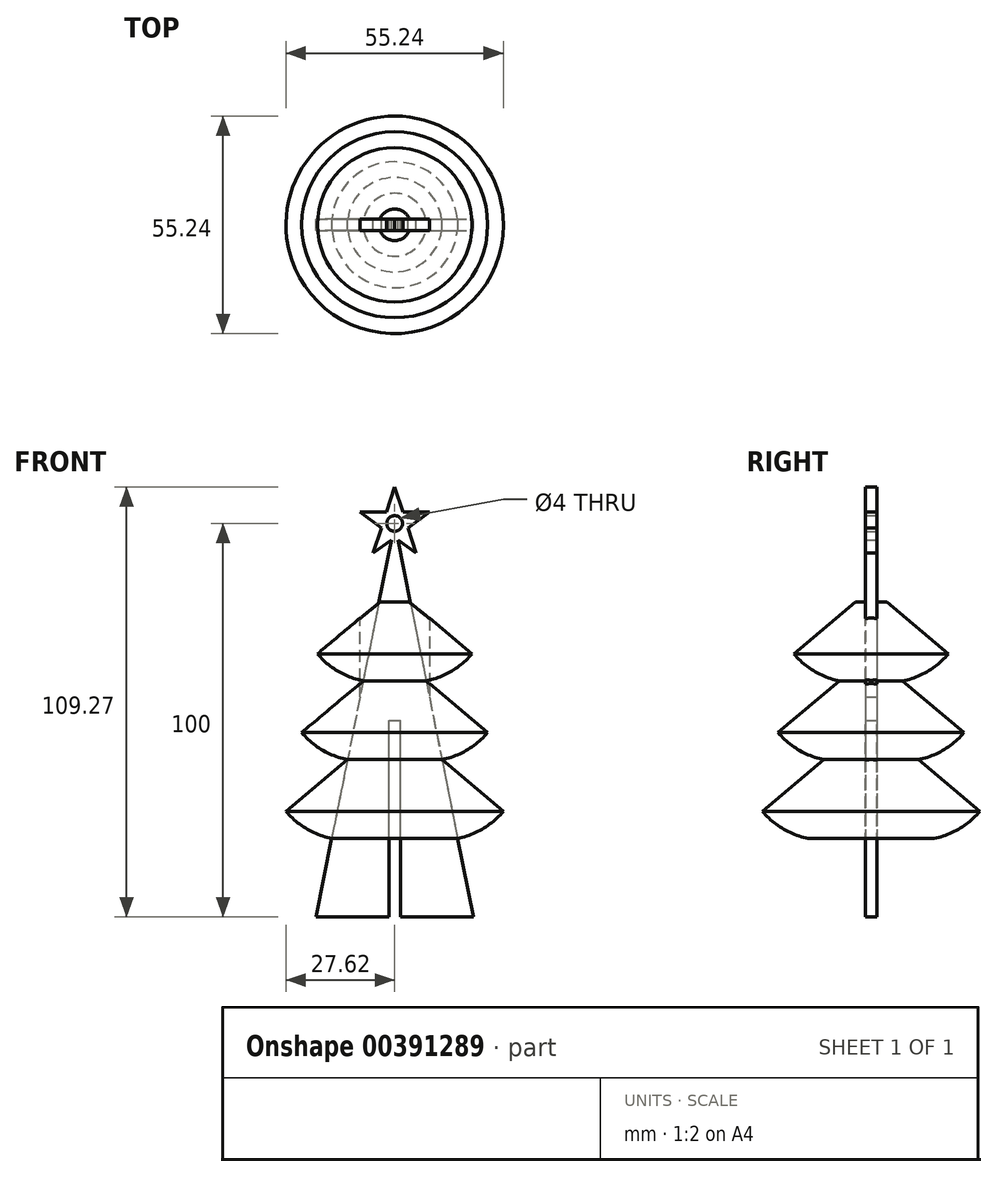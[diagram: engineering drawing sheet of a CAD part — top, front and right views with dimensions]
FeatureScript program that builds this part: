
annotation { "Feature Type Name" : "Feature", "Feature Type Description" : "" }
export const myFeature = defineFeature(function(context is Context, id is Id, definition is map)
    precondition{}
    {
        {
            var Q0;
            Q0=qCreatedBy(makeId("Front.planeOp"),FACE);
            var sketch = newSketch(context, id + "F0", { "sketchPlane" : qUnion([Q0])});
            skLineSegment(sketch, "E0", {"start": v(-20, 0) * mm, "end": v(-1.5, 0) * mm});
            skCircle(sketch, "E1.cCircle", {"center": v(0, 100) * mm, "radius": 7.5 * mm, "construction": true});
            skLineSegment(sketch, "E1.4", {"start": v(7.13, 97.68) * mm, "end": v(5.45, 92.5) * mm});
            skPoint(sketch, "E1.0.midPoint", {"position": v(0, 92.5) * mm});
            skLineSegment(sketch, "E2", {"start": v(-5.45, 92.5) * mm, "end": v(-3.37, 98.9) * mm});
            skLineSegment(sketch, "E3", {"start": v(0, 109.27) * mm, "end": v(2.08, 102.86) * mm});
            skLineSegment(sketch, "E4", {"start": v(-8.82, 102.86) * mm, "end": v(-2.08, 102.86) * mm});
            skLineSegment(sketch, "E5", {"start": v(-5.45, 92.5) * mm, "end": v(-0.83, 95.86) * mm});
            skLineSegment(sketch, "E6", {"start": v(-8.82, 102.86) * mm, "end": v(-3.37, 98.9) * mm});
            skLineSegment(sketch, "E7.trimOffspring", {"start": v(2.08, 102.86) * mm, "end": v(8.82, 102.86) * mm});
            skLineSegment(sketch, "E8.trimOffspring", {"start": v(3.37, 98.9) * mm, "end": v(5.45, 92.5) * mm});
            skLineSegment(sketch, "E9.trimOffspring", {"start": v(3.37, 98.9) * mm, "end": v(8.82, 102.86) * mm});
            skLineSegment(sketch, "E10.trimOffspring", {"start": v(0.83, 95.86) * mm, "end": v(5.45, 92.5) * mm});
            skLineSegment(sketch, "E11.trimOffspring", {"start": v(-0.83, 95.86) * mm, "end": v(-20, 0) * mm});
            skLineSegment(sketch, "E12.trimOffspring", {"start": v(0.83, 95.86) * mm, "end": v(20, 0) * mm});
            skLineSegment(sketch, "E13.trimOffspring", {"start": v(-2.08, 102.86) * mm, "end": v(0, 109.27) * mm});
            skCircle(sketch, "E14", {"center": v(0, 100) * mm, "radius": 2 * mm});
            skLineSegment(sketch, "E15.0", {"start": v(1.5, 0) * mm, "end": v(1.5, 50) * mm});
            skLineSegment(sketch, "E16.MirrorCS", {"start": v(-1.5, 0) * mm, "end": v(-1.5, 50) * mm});
            skLineSegment(sketch, "E17", {"start": v(-1.5, 50) * mm, "end": v(1.5, 50) * mm});
            skLineSegment(sketch, "E18.trimOffspring", {"start": v(1.5, 0) * mm, "end": v(20, 0) * mm});
            skSolve(sketch);
        }
        {
            var Q0;
            Q0 = qSketchRegion(id + "F0", true);
            extrude(context, id + "F1", {"entities" : qUnion([Q0]), "endBound" : BoundingType.SYMMETRIC, "depth" : 3 * mm});
        }
        {
            var Q0;
            Q0=qCreatedBy(makeId("Right.planeOp"),FACE);
            var sketch = newSketch(context, id + "F2", { "sketchPlane" : qUnion([Q0])});
            skLineSegment(sketch, "E19", {"start": v(-20, 0) * mm, "end": v(0, 100) * mm});
            skLineSegment(sketch, "E20.MirrorCS", {"start": v(20, 0) * mm, "end": v(0, 100) * mm});
            skLineSegment(sketch, "E21", {"start": v(-20, 0) * mm, "end": v(20, 0) * mm});
            skSolve(sketch);
        }
        {
            var Q0;
            Q0 = qSketchRegion(id + "F2", true);
            extrude(context, id + "F3", {"entities" : qUnion([Q0]), "endBound" : BoundingType.SYMMETRIC, "depth" : 3 * mm});
        }
        {
            var Q0;
            Q0=makeQuery(id+"F1.opExtrude","SWEPT_BODY",BODY,{"disambiguationData":[OSD([sQuery(id+"F0.wireOp",EDGE,"E0"),sQuery(id+"F0.wireOp",EDGE,"E2"),sQuery(id+"F0.wireOp",EDGE,"E3"),sQuery(id+"F0.wireOp",EDGE,"E4"),sQuery(id+"F0.wireOp",EDGE,"E5"),sQuery(id+"F0.wireOp",EDGE,"E6"),sQuery(id+"F0.wireOp",EDGE,"E7.trimOffspring"),sQuery(id+"F0.wireOp",EDGE,"E8.trimOffspring"),sQuery(id+"F0.wireOp",EDGE,"E9.trimOffspring"),sQuery(id+"F0.wireOp",EDGE,"E10.trimOffspring"),sQuery(id+"F0.wireOp",EDGE,"E11.trimOffspring"),sQuery(id+"F0.wireOp",EDGE,"E12.trimOffspring"),sQuery(id+"F0.wireOp",EDGE,"E13.trimOffspring"),sQuery(id+"F0.wireOp",EDGE,"E14"),sQuery(id+"F0.wireOp",EDGE,"E15.0"),sQuery(id+"F0.wireOp",EDGE,"E16.MirrorCS"),sQuery(id+"F0.wireOp",EDGE,"E17"),sQuery(id+"F0.wireOp",EDGE,"E18.trimOffspring")])]});
            var Q1;
            Q1=makeQuery(id+"F3.opExtrude","SWEPT_BODY",BODY,{"disambiguationData":[OSD([sQuery(id+"F2.wireOp",EDGE,"E19"),sQuery(id+"F2.wireOp",EDGE,"E20.MirrorCS"),sQuery(id+"F2.wireOp",EDGE,"E21")])]});
            booleanBodies(context, id + "F4", {"operationType" : BooleanOperationType.SUBTRACTION, "tools" : qUnion([Q0]), "targets" : qUnion([Q1]), "keepTools" : true});
        }
        {
            var Q0;
            Q0=makeQuery(id+"F4.opBoolean","SPLIT",BODY,{"disambiguationData":[OD(0.0)],"derivedFrom":makeQuery(id+"F3.opExtrude","SWEPT_BODY",BODY,{"disambiguationData":[OSD([sQuery(id+"F2.wireOp",EDGE,"E19"),sQuery(id+"F2.wireOp",EDGE,"E20.MirrorCS"),sQuery(id+"F2.wireOp",EDGE,"E21")])]})});
            var Q1;
            Q1=makeQuery(id+"F4.opBoolean","SPLIT",BODY,{"disambiguationData":[OD(1.0)],"derivedFrom":makeQuery(id+"F3.opExtrude","SWEPT_BODY",BODY,{"disambiguationData":[OSD([sQuery(id+"F2.wireOp",EDGE,"E19"),sQuery(id+"F2.wireOp",EDGE,"E20.MirrorCS"),sQuery(id+"F2.wireOp",EDGE,"E21")])]})});
            var Q2;
            Q2=makeQuery(id+"F4.opBoolean","SPLIT",BODY,{"disambiguationData":[OD(3.0)],"derivedFrom":makeQuery(id+"F3.opExtrude","SWEPT_BODY",BODY,{"disambiguationData":[OSD([sQuery(id+"F2.wireOp",EDGE,"E19"),sQuery(id+"F2.wireOp",EDGE,"E20.MirrorCS"),sQuery(id+"F2.wireOp",EDGE,"E21")])]})});
            deleteBodies(context, id + "F5", {"entities" : qUnion([Q0, Q1, Q2])});
        }
        {
            var Q0;
            Q0=qCreatedBy(makeId("Front.planeOp"),FACE);
            var sketch = newSketch(context, id + "F6", { "sketchPlane" : qUnion([Q0])});
            skLineSegment(sketch, "E22.0.2", {"start": v(-20, 0) * mm, "end": v(-0.83, 95.86) * mm});
            skLineSegment(sketch, "E23", {"start": v(0, 20) * mm, "end": v(-16, 20) * mm});
            skLineSegment(sketch, "E24.0", {"start": v(0, 40) * mm, "end": v(-12, 40) * mm});
            skArc(sketch, "E25", {"start": v(-27.62, 26.89) * mm, "mid": v(-22.4, 22.45) * mm, "end": v(-16, 20) * mm});
            skLineSegment(sketch, "E26", {"start": v(-12, 40) * mm, "end": v(-27.62, 26.89) * mm});
            skLineSegment(sketch, "E27", {"start": v(0, 40) * mm, "end": v(0, 20) * mm});
            skPoint(sketch, "E28.orphan", {"position": v(-0.83, 95.86) * mm});
            skPoint(sketch, "E22.0.0.end.orphan", {"position": v(-20, 0) * mm});
            skSolve(sketch);
        }
        {
            var Q0;
            Q0 = qSketchRegion(id + "F6", true);
            var Q1;
            Q1=sQuery(id+"F6.wireOp",EDGE,"E27");
            revolve(context, id + "F7", {"entities" : qUnion([Q0]), "axis" : qUnion([Q1]), "revolveType" : RevolveType.FULL});
        }
        {
            var Q0;
            Q0=qCreatedBy(makeId("Front.planeOp"),FACE);
            var sketch = newSketch(context, id + "F8", { "sketchPlane" : qUnion([Q0])});
            skLineSegment(sketch, "E29.0", {"start": v(-20, 0) * mm, "end": v(-0.83, 95.86) * mm});
            skLineSegment(sketch, "E30.0.0", {"start": v(-12, 40) * mm, "end": v(0, 40) * mm});
            skLineSegment(sketch, "E31.0", {"start": v(-8, 60) * mm, "end": v(0, 60) * mm});
            skLineSegment(sketch, "E32", {"start": v(0, 40) * mm, "end": v(0, 60) * mm});
            skArc(sketch, "E33", {"start": v(-23.62, 46.89) * mm, "mid": v(-18.4, 42.45) * mm, "end": v(-12, 40) * mm});
            skLineSegment(sketch, "E34", {"start": v(-8, 60) * mm, "end": v(-23.62, 46.89) * mm});
            skSolve(sketch);
        }
        {
            var Q0;
            Q0 = qSketchRegion(id + "F8", true);
            var Q1;
            Q1=sQuery(id+"F8.wireOp",EDGE,"E32");
            revolve(context, id + "F9", {"entities" : qUnion([Q0]), "axis" : qUnion([Q1]), "revolveType" : RevolveType.FULL});
        }
        {
            var Q0;
            Q0=qCreatedBy(makeId("Front.planeOp"),FACE);
            var sketch = newSketch(context, id + "F10", { "sketchPlane" : qUnion([Q0])});
            skLineSegment(sketch, "E35.0.0", {"start": v(20, 0) * mm, "end": v(0.83, 95.86) * mm});
            skLineSegment(sketch, "E35.0.2", {"start": v(0.83, 95.86) * mm, "end": v(20, 0) * mm});
            skLineSegment(sketch, "E36.0.0", {"start": v(0, 60) * mm, "end": v(8, 60) * mm});
            skLineSegment(sketch, "E37.0", {"start": v(0, 80) * mm, "end": v(4, 80) * mm});
            skLineSegment(sketch, "E38", {"start": v(0, 60) * mm, "end": v(0, 80) * mm});
            skArc(sketch, "E39", {"start": v(8, 60) * mm, "mid": v(14.4, 62.45) * mm, "end": v(19.62, 66.89) * mm});
            skLineSegment(sketch, "E40", {"start": v(4, 80) * mm, "end": v(19.62, 66.89) * mm});
            skSolve(sketch);
        }
        {
            var Q0;
            Q0 = qSketchRegion(id + "F10", true);
            var Q1;
            Q1=sQuery(id+"F10.wireOp",EDGE,"E38");
            revolve(context, id + "F11", {"entities" : qUnion([Q0]), "axis" : qUnion([Q1]), "revolveType" : RevolveType.FULL});
        }
        {
            var Q0;
            Q0=makeQuery(id+"F1.opExtrude","SWEPT_BODY",BODY,{"disambiguationData":[OSD([sQuery(id+"F0.wireOp",EDGE,"E0"),sQuery(id+"F0.wireOp",EDGE,"E2"),sQuery(id+"F0.wireOp",EDGE,"E3"),sQuery(id+"F0.wireOp",EDGE,"E4"),sQuery(id+"F0.wireOp",EDGE,"E5"),sQuery(id+"F0.wireOp",EDGE,"E6"),sQuery(id+"F0.wireOp",EDGE,"E7.trimOffspring"),sQuery(id+"F0.wireOp",EDGE,"E8.trimOffspring"),sQuery(id+"F0.wireOp",EDGE,"E9.trimOffspring"),sQuery(id+"F0.wireOp",EDGE,"E10.trimOffspring"),sQuery(id+"F0.wireOp",EDGE,"E11.trimOffspring"),sQuery(id+"F0.wireOp",EDGE,"E12.trimOffspring"),sQuery(id+"F0.wireOp",EDGE,"E13.trimOffspring"),sQuery(id+"F0.wireOp",EDGE,"E14"),sQuery(id+"F0.wireOp",EDGE,"E15.0"),sQuery(id+"F0.wireOp",EDGE,"E16.MirrorCS"),sQuery(id+"F0.wireOp",EDGE,"E17"),sQuery(id+"F0.wireOp",EDGE,"E18.trimOffspring")])]});
            var Q1;
            Q1=makeQuery(id+"F4.opBoolean","SPLIT",BODY,{"disambiguationData":[OD(2.0)],"derivedFrom":makeQuery(id+"F3.opExtrude","SWEPT_BODY",BODY,{"disambiguationData":[OSD([sQuery(id+"F2.wireOp",EDGE,"E19"),sQuery(id+"F2.wireOp",EDGE,"E20.MirrorCS"),sQuery(id+"F2.wireOp",EDGE,"E21")])]})});
            var Q2;
            Q2=makeQuery(id+"F11.opRevolve","SWEPT_BODY",BODY,{"disambiguationData":[OSD([sQuery(id+"F10.wireOp",EDGE,"E36.0.0"),sQuery(id+"F10.wireOp",EDGE,"E37.0"),sQuery(id+"F10.wireOp",EDGE,"E38"),sQuery(id+"F10.wireOp",EDGE,"E39"),sQuery(id+"F10.wireOp",EDGE,"E40")])]});
            var Q3;
            Q3=makeQuery(id+"F9.opRevolve","SWEPT_BODY",BODY,{"disambiguationData":[OSD([sQuery(id+"F8.wireOp",EDGE,"E30.0.0"),sQuery(id+"F8.wireOp",EDGE,"E31.0"),sQuery(id+"F8.wireOp",EDGE,"E32"),sQuery(id+"F8.wireOp",EDGE,"E33"),sQuery(id+"F8.wireOp",EDGE,"E34")])]});
            var Q4;
            Q4=makeQuery(id+"F7.opRevolve","SWEPT_BODY",BODY,{"disambiguationData":[OSD([sQuery(id+"F6.wireOp",EDGE,"E23"),sQuery(id+"F6.wireOp",EDGE,"E24.0"),sQuery(id+"F6.wireOp",EDGE,"E25"),sQuery(id+"F6.wireOp",EDGE,"E26"),sQuery(id+"F6.wireOp",EDGE,"E27")])]});
            booleanBodies(context, id + "F12", {"operationType" : BooleanOperationType.SUBTRACTION, "tools" : qUnion([Q0, Q1]), "targets" : qUnion([Q2, Q3, Q4]), "keepTools" : true});
        }
        {
            var Q0;
            Q0=qCreatedBy(makeId("Front.planeOp"),FACE);
            var sketch = newSketch(context, id + "F13", { "sketchPlane" : qUnion([Q0])});
            skPoint(sketch, "E41.0", {"position": v(8.82, 102.86) * mm});
            skPoint(sketch, "E42.0", {"position": v(-8.82, 102.86) * mm});
            skLineSegment(sketch, "E43", {"start": v(8.82, 102.86) * mm, "end": v(8.82, 0) * mm});
            skLineSegment(sketch, "E44", {"start": v(8.82, 0) * mm, "end": v(-8.82, 0) * mm});
            skLineSegment(sketch, "E45", {"start": v(-8.82, 0) * mm, "end": v(-8.82, 102.86) * mm});
            skLineSegment(sketch, "E46", {"start": v(-8.82, 102.86) * mm, "end": v(8.82, 102.86) * mm});
            skSolve(sketch);
        }
        {
            var Q0;
            Q0 = qSketchRegion(id + "F13", true);
            extrude(context, id + "F14", {"entities" : qUnion([Q0]), "endBound" : BoundingType.SYMMETRIC, "depth" : 3 * mm});
        }
        {
            var Q0;
            Q0=makeQuery(id+"F14.opExtrude","SWEPT_BODY",BODY,{"disambiguationData":[OSD([sQuery(id+"F13.wireOp",EDGE,"E43"),sQuery(id+"F13.wireOp",EDGE,"E44"),sQuery(id+"F13.wireOp",EDGE,"E45"),sQuery(id+"F13.wireOp",EDGE,"E46")])]});
            var Q1;
            Q1=makeQuery(id+"F11.opRevolve","SWEPT_BODY",BODY,{"disambiguationData":[OSD([sQuery(id+"F10.wireOp",EDGE,"E36.0.0"),sQuery(id+"F10.wireOp",EDGE,"E37.0"),sQuery(id+"F10.wireOp",EDGE,"E38"),sQuery(id+"F10.wireOp",EDGE,"E39"),sQuery(id+"F10.wireOp",EDGE,"E40")])]});
            var Q2;
            Q2=makeQuery(id+"F9.opRevolve","SWEPT_BODY",BODY,{"disambiguationData":[OSD([sQuery(id+"F8.wireOp",EDGE,"E30.0.0"),sQuery(id+"F8.wireOp",EDGE,"E31.0"),sQuery(id+"F8.wireOp",EDGE,"E32"),sQuery(id+"F8.wireOp",EDGE,"E33"),sQuery(id+"F8.wireOp",EDGE,"E34")])]});
            var Q3;
            Q3=makeQuery(id+"F7.opRevolve","SWEPT_BODY",BODY,{"disambiguationData":[OSD([sQuery(id+"F6.wireOp",EDGE,"E23"),sQuery(id+"F6.wireOp",EDGE,"E24.0"),sQuery(id+"F6.wireOp",EDGE,"E25"),sQuery(id+"F6.wireOp",EDGE,"E26"),sQuery(id+"F6.wireOp",EDGE,"E27")])]});
            booleanBodies(context, id + "F15", {"operationType" : BooleanOperationType.SUBTRACTION, "tools" : qUnion([Q0]), "targets" : qUnion([Q1, Q2, Q3])});
        }
    });
